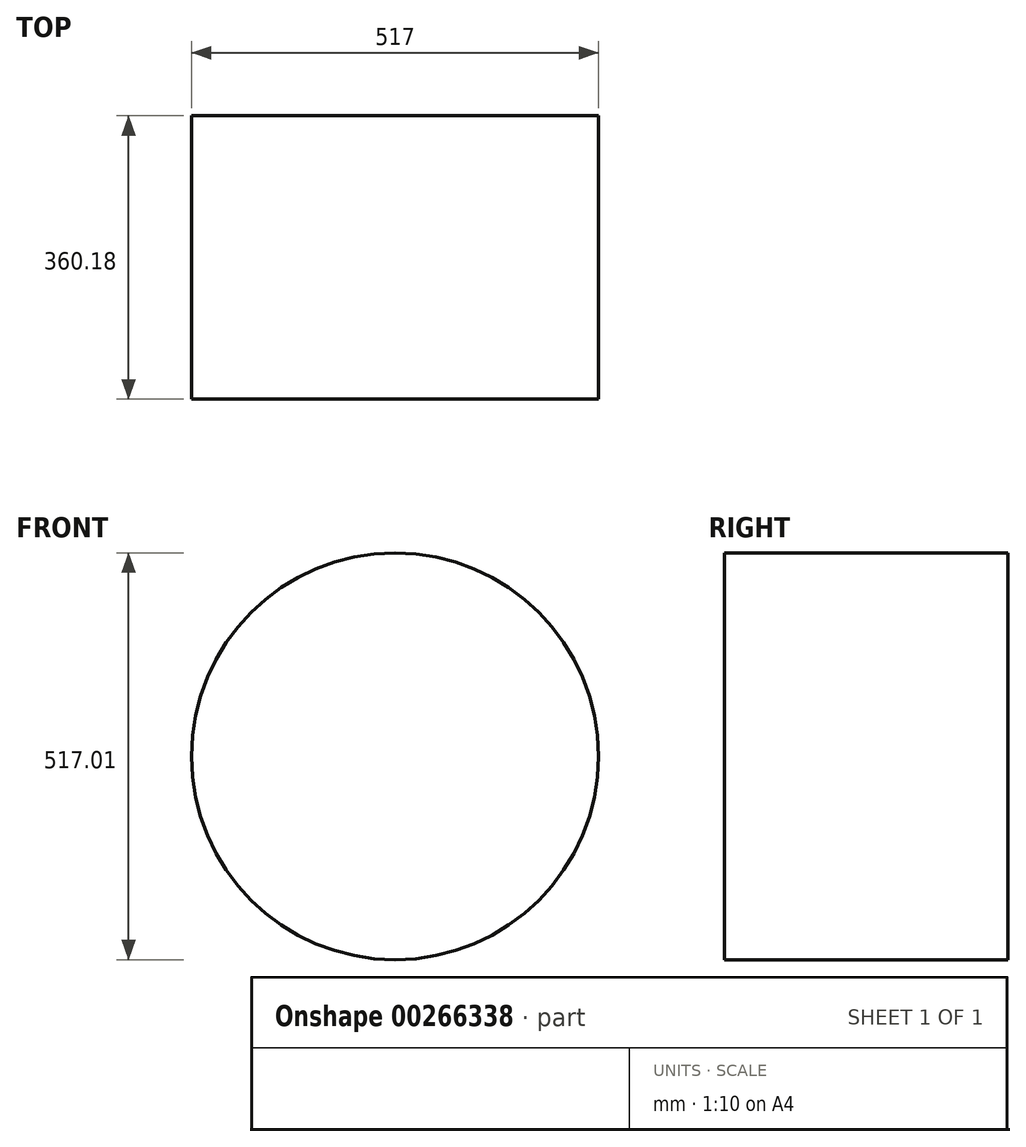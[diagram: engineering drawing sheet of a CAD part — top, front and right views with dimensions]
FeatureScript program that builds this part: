
annotation { "Feature Type Name" : "Feature", "Feature Type Description" : "" }
export const myFeature = defineFeature(function(context is Context, id is Id, definition is map)
    precondition{}
    {
        {
            var Q0;
            Q0=qCreatedBy(makeId("Front.planeOp"),FACE);
            var sketch = newSketch(context, id + "F0", { "sketchPlane" : qUnion([Q0])});
            skCircle(sketch, "E0", {"center": v(-111.39, 79.58) * mm, "radius": 258.5 * mm});
            skSolve(sketch);
        }
        {
            var Q0;
            Q0=makeQuery(id+"F0.imprint","IMPRINT",FACE,{"disambiguationData":[TD([[makeQuery(id+"F0.imprint","IMPRINT",EDGE,{"derivedFrom":sQuery(id+"F0.wireOp",EDGE,"E0")}),1.0]])]});
            extrude(context, id + "F1", {"entities" : qUnion([Q0]), "endBound" : BoundingType.SYMMETRIC, "depth" : 360.17 * mm});
        }
    });
